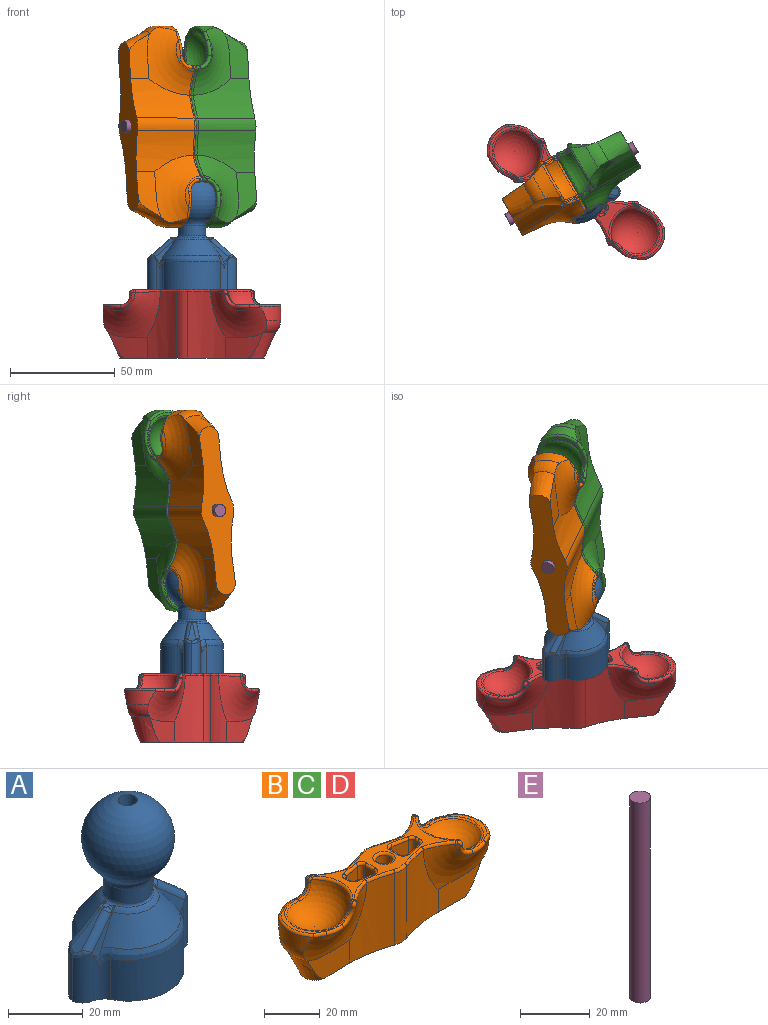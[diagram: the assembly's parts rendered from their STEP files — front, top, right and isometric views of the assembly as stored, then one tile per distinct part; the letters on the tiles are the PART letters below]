
ASSEMBLY  parts=5 mates=4
PART A: 86 faces, bbox 42.8x30.4x55.8 mm
  f0: plane 12.56x10.39mm, normal (0,-0.98,0.19), area 21.3mm2, adj f16,f23,f29,f42,f45,f46,f71,f72
  f1: plane 12.56x10.39mm, normal (0,0.98,0.19), area 21.3mm2, adj f13,f24,f32,f40,f61,f62,f79,f80
  f2: plane 1.84x1.78mm, normal (0,0,1), area 2.6mm2, adj f22,f46,f47,f48,f49,f50
  f3: bspline ~18.33x15.88mm, area 330.1mm2, adj f5,f8,f9,f11
  f4: bspline ~18.33x15.88mm, area 304.7mm2, adj f5,f8,f9,f11
  f5: cylinder r=6.94mm len=14.55mm, axis (0,0,-1), area 174.4mm2, adj f3,f4,f9,f11
  f6: cylinder r=15mm len=26.79mm, axis (0,0,-1), area 441.6mm2, adj f10,f25,f26,f33
  f7: cylinder r=15mm len=26.79mm, axis (0,0,-1), area 441.6mm2, adj f10,f27,f28,f30
  f8: cylinder r=7.94mm len=15.88mm, axis (0,0,-1), area 333.9mm2, adj f3,f4,f9,f10,f11
  f9: plane 1.5x1mm, normal (0,-1,0), area 1.1mm2, adj f3,f4,f5,f8
  f10: plane 42.34x30mm, normal (0,0,-1), area 600.2mm2, adj f6,f7,f8,f25,f26,f27,f28,f35
  f11: plane 15.57x15.31mm, normal (0,0,-1), area 176.5mm2, adj f3,f4,f5,f8
  f12: plane 1.98x1.91mm, normal (0,0,1), area 2.6mm2, adj f22,f57,f58,f59,f60,f61
  f13: bspline ~28.91x12.94mm, area 275.1mm2, adj f1,f18,f24,f32,f33,f34
  f14: plane 10.41x9.05mm, normal (-0.66,0,0.75), area 28.4mm2, adj f39,f40,f59,f76,f77
  f15: plane 12.57x10.39mm, normal (0,-0.98,0.19), area 21.3mm2, adj f16,f23,f31,f39,f56,f57,f73,f74
  f16: bspline ~28.91x12.94mm, area 275.1mm2, adj f0,f15,f23,f29,f30,f31
  f17: plane 10.41x9.05mm, normal (0.66,0,0.75), area 28.4mm2, adj f41,f42,f48,f68,f69
  f18: plane 12.57x10.39mm, normal (0,0.98,0.19), area 21.3mm2, adj f13,f24,f34,f41,f50,f51,f65,f66
  f19: cylinder r=6.5mm len=13mm, axis (0,0,-1), area 191.6mm2, adj f21,f22
  f20: sphere r=12.5mm, area 1728.4mm2, adj f21,f81
  f21: torus R=9.9mm, axis (0,0,1), area 133.2mm2, adj f19,f20
  f22: torus R=7.44mm, axis (0,0,1), area 43.2mm2, adj f2,f12,f19,f23,f24,f43,f44,f45
  f23: bspline ~16.51x7.87mm, area 37.6mm2, adj f0,f15,f16,f22,f43,f44,f54,f55
  f24: bspline ~16.51x7.87mm, area 37.6mm2, adj f1,f13,f18,f22,f52,f53,f63,f64
  f25: cylinder r=5mm len=14.41mm, axis (0,0,-1), area 56.2mm2, adj f6,f10,f34,f35,f65
  f26: cylinder r=5mm len=14.41mm, axis (0,0,-1), area 56.2mm2, adj f6,f10,f32,f38,f80
  f27: cylinder r=5mm len=14.41mm, axis (0,0,-1), area 56.2mm2, adj f7,f10,f31,f37,f73
  f28: cylinder r=5mm len=14.41mm, axis (0,0,-1), area 56.2mm2, adj f7,f10,f29,f36,f72
  f29: bspline ~6.67x5.77mm, area 12.8mm2, adj f0,f16,f28,f30,f72
  f30: bspline ~27.53x9.91mm, area 104.2mm2, adj f7,f16,f29,f31
  f31: bspline ~6.67x5.77mm, area 12.8mm2, adj f15,f16,f27,f30,f73
  f32: bspline ~6.67x5.77mm, area 12.8mm2, adj f1,f13,f26,f33,f80
  f33: bspline ~27.53x9.91mm, area 104.2mm2, adj f6,f13,f32,f34
  f34: bspline ~6.67x5.77mm, area 12.8mm2, adj f13,f18,f25,f33,f65
  f35: cylinder r=5mm len=15.46mm, axis (0,0,-1), area 92.6mm2, adj f10,f25,f36,f66,f67,f68
  f36: cylinder r=5mm len=15.46mm, axis (0,0,-1), area 92.6mm2, adj f10,f28,f35,f69,f70,f71
  f37: cylinder r=5mm len=15.46mm, axis (0,0,-1), area 92.6mm2, adj f10,f27,f38,f74,f75,f76
  f38: cylinder r=5mm len=15.46mm, axis (0,0,-1), area 92.6mm2, adj f10,f26,f37,f77,f78,f79
  f39: cylinder r=2.17mm len=11.07mm, axis (-0.75,-0.13,-0.65), area 38.1mm2, adj f14,f15,f58,f75
  f40: cylinder r=2.17mm len=11.07mm, axis (0.75,-0.13,0.65), area 38.1mm2, adj f1,f14,f60,f78
  f41: cylinder r=2.17mm len=11.07mm, axis (-0.75,-0.13,0.65), area 38.1mm2, adj f17,f18,f49,f67
  f42: cylinder r=2.17mm len=11.07mm, axis (0.75,-0.13,-0.65), area 38.1mm2, adj f0,f17,f47,f70
  f43: bspline ~0.78x0.75mm, area 0.1mm2, adj f22,f23,f44
  f44: bspline ~0.96x0.73mm, area 0.2mm2, adj f22,f23,f43,f45
  f45: bspline ~1.46x1.03mm, area 0.5mm2, adj f0,f22,f44,f46
  f46: bspline ~1.57x1.46mm, area 1.4mm2, adj f0,f2,f45,f47
  f47: bspline ~2.07x1.82mm, area 3.1mm2, adj f2,f42,f46,f48
  f48: cylinder r=1.57mm len=1.03mm, axis (0,-1,0), area 0.5mm2, adj f2,f17,f47,f49
  f49: bspline ~2.22x2.15mm, area 3.1mm2, adj f2,f41,f48,f50
  f50: bspline ~1.54x1.27mm, area 1.4mm2, adj f2,f18,f49,f51
  f51: bspline ~1.46x1.03mm, area 0.5mm2, adj f18,f22,f50,f52
  f52: bspline ~0.96x0.73mm, area 0.2mm2, adj f22,f24,f51,f53
  f53: bspline ~1x0.94mm, area 0.1mm2, adj f22,f24,f52
  f54: bspline ~1x0.94mm, area 0.1mm2, adj f22,f23,f55
  f55: bspline ~0.96x0.73mm, area 0.2mm2, adj f22,f23,f54,f56
  f56: bspline ~1.46x1.03mm, area 0.5mm2, adj f15,f22,f55,f57
  f57: bspline ~1.56x1.37mm, area 1.4mm2, adj f12,f15,f56,f58
  f58: bspline ~2.15x1.82mm, area 3.1mm2, adj f12,f39,f57,f59
  f59: cylinder r=1.57mm len=1.03mm, axis (0,-1,0), area 0.5mm2, adj f12,f14,f58,f60
  f60: bspline ~2.22x2.15mm, area 3.1mm2, adj f12,f40,f59,f61
  f61: bspline ~1.57x1.48mm, area 1.4mm2, adj f1,f12,f60,f62
  f62: bspline ~1.46x1.03mm, area 0.5mm2, adj f1,f22,f61,f63
  f63: bspline ~0.96x0.73mm, area 0.2mm2, adj f22,f24,f62,f64
  f64: bspline ~0.78x0.75mm, area 0.1mm2, adj f22,f24,f63
  f65: bspline ~8.8x3.81mm, area 2.3mm2, adj f18,f25,f34,f66
  f66: bspline ~1.36x1.32mm, area 0.8mm2, adj f18,f35,f65,f67
  f67: bspline ~2.98x2.85mm, area 2.6mm2, adj f35,f41,f66,f68
  f68: bspline ~3.29x2.24mm, area 4.8mm2, adj f17,f35,f67,f69
  f69: bspline ~3.29x2.24mm, area 4.8mm2, adj f17,f36,f68,f70
  f70: bspline ~2.98x2.85mm, area 2.6mm2, adj f36,f42,f69,f71
  f71: bspline ~1.36x1.32mm, area 0.8mm2, adj f0,f36,f70,f72
  f72: bspline ~8.8x3.81mm, area 2.3mm2, adj f0,f28,f29,f71
  f73: bspline ~8.8x3.81mm, area 2.3mm2, adj f15,f27,f31,f74
  f74: bspline ~1.36x1.32mm, area 0.8mm2, adj f15,f37,f73,f75
  f75: bspline ~2.98x2.85mm, area 2.6mm2, adj f37,f39,f74,f76
  f76: bspline ~3.29x2.24mm, area 4.8mm2, adj f14,f37,f75,f77
  f77: bspline ~3.29x2.24mm, area 4.8mm2, adj f14,f38,f76,f78
  f78: bspline ~2.98x2.85mm, area 2.6mm2, adj f38,f40,f77,f79
  f79: bspline ~1.36x1.32mm, area 0.8mm2, adj f1,f38,f78,f80
  f80: bspline ~8.8x3.81mm, area 2.3mm2, adj f1,f26,f32,f79
  f81: cone r=2.85mm half-angle=3.8deg, axis (0,0,1), area 77.3mm2, adj f20,f82
  f82: sphere r=7.5mm, area 685.5mm2, adj f81,f83
  f83: cone r=2.85mm half-angle=3.8deg, axis (0,0,1), area 75.2mm2, adj f82,f84
  f84: cone r=0.13mm half-angle=0.1deg, axis (0,0,1), area 5.8mm2, adj f83,f85
  f85: sphere r=7.5mm, area 0mm2, adj f84
PART B: 146 faces, bbox 113x30x32.8 mm
  f0: sphere r=15mm, area 23.2mm2, adj f22,f89,f91,f93,f95,f97
  f1: sphere r=15mm, area 23.2mm2, adj f20,f109,f110,f111,f112,f113
  f2: sphere r=12.5mm, area 560.4mm2, adj f114,f115,f116,f117,f118,f119,f120,f121
  f3: sphere r=15mm, area 23.2mm2, adj f23,f78,f79,f80,f81,f82
  f4: sphere r=15mm, area 23.2mm2, adj f21,f94,f96,f98,f100,f102
  f5: sphere r=12.5mm, area 560.4mm2, adj f70,f71,f72,f73,f74,f75,f76,f77
  f6: cylinder r=9mm len=31.5mm, axis (0,0,-1), area 196.5mm2, adj f24,f26,f103,f143
  f7: cylinder r=13.27mm len=18.19mm, axis (0,0,-1), area 103mm2, adj f18,f22,f23,f83,f85,f87
  f8: cylinder r=9mm len=31.5mm, axis (0,0,-1), area 196.5mm2, adj f25,f27,f88,f143
  f9: cylinder r=13.27mm len=18.19mm, axis (0,0,-1), area 103mm2, adj f19,f20,f21,f104,f106,f108
  f10: cylinder r=3mm len=31.5mm, axis (0,0,-1), area 593.8mm2, adj f138,f143
  f11: plane 52.62x21.86mm, normal (0,0,1), area 310.7mm2, adj f66,f67,f68,f69,f74,f82,f84,f86
  f12: plane 0.68x0.31mm, normal (1,0,0), area 0.2mm2, adj f30,f68,f70,f98
  f13: plane 0.68x0.31mm, normal (1,0,0), area 0.2mm2, adj f29,f67,f77,f113
  f14: plane 22.98x14.27mm, normal (0,0,1), area 40.1mm2, adj f29,f30,f73,f102,f104,f106,f108,f110
  f15: plane 0.68x0.31mm, normal (-1,0,0), area 0.2mm2, adj f31,f69,f93,f121
  f16: plane 0.68x0.31mm, normal (-1,0,0), area 0.2mm2, adj f28,f66,f78,f114
  f17: plane 22.98x14.27mm, normal (0,0,1), area 40.1mm2, adj f28,f31,f81,f83,f85,f87,f89,f118
  f18: torus R=5.27mm, axis (0,0,1), area 77.7mm2, adj f7,f22,f23,f144
  f19: torus R=5.27mm, axis (0,0,1), area 77.7mm2, adj f9,f20,f21,f145
  f20: torus R=26.08mm, axis (0,-1,0), area 502.5mm2, adj f1,f9,f19,f26,f107,f108,f141,f145
  f21: torus R=26.08mm, axis (0,-1,0), area 502.5mm2, adj f4,f9,f19,f27,f92,f104,f142,f145
  f22: torus R=26.08mm, axis (0,-1,0), area 502.5mm2, adj f0,f7,f18,f24,f87,f99,f140,f144
  f23: torus R=26.08mm, axis (0,-1,0), area 502.5mm2, adj f3,f7,f18,f25,f83,f84,f139,f144
  f24: cylinder r=58.26mm len=31.5mm, axis (0,0,-1), area 507.2mm2, adj f6,f22,f99,f101,f140,f143
  f25: cylinder r=58.26mm len=31.5mm, axis (0,0,-1), area 507.2mm2, adj f8,f23,f84,f86,f139,f143
  f26: cylinder r=58.26mm len=31.5mm, axis (0,0,-1), area 507.2mm2, adj f6,f20,f105,f107,f141,f143
  f27: cylinder r=58.26mm len=31.5mm, axis (0,0,-1), area 507.2mm2, adj f8,f21,f90,f92,f142,f143
  f28: cylinder r=5mm len=5mm, axis (0,1,0), area 5mm2, adj f16,f17,f79,f116
  f29: cylinder r=5mm len=5mm, axis (0,-1,0), area 5mm2, adj f13,f14,f76,f112
  f30: cylinder r=5mm len=5mm, axis (0,-1,0), area 5mm2, adj f12,f14,f71,f100
  f31: cylinder r=5mm len=5mm, axis (0,1,0), area 5mm2, adj f15,f17,f91,f120
  f32: plane 12.31x7.2mm, normal (-0.19,0.98,0), area 90.3mm2, adj f44,f50,f53,f135
  f33: plane 12.31x1.56mm, normal (-1,0,0), area 19.2mm2, adj f47,f51,f53,f131
  f34: plane 12.31x7.2mm, normal (-0.19,-0.98,0), area 90.3mm2, adj f42,f46,f47,f132
  f35: plane 12.31x4.39mm, normal (1,0,0), area 54mm2, adj f42,f44,f45,f136
  f36: plane 7.2x4.39mm, normal (0,0,1), area 21.4mm2, adj f45,f46,f50,f51
  f37: plane 12.31x7.2mm, normal (0.19,-0.98,0), area 90.3mm2, adj f59,f63,f65,f128
  f38: plane 12.31x1.56mm, normal (1,0,0), area 19.2mm2, adj f54,f58,f59,f127
  f39: plane 12.31x7.2mm, normal (0.19,0.98,0), area 90.3mm2, adj f54,f56,f57,f123
  f40: plane 12.31x4.39mm, normal (-1,0,0), area 54mm2, adj f56,f62,f65,f124
  f41: plane 7.2x4.39mm, normal (0,0,1), area 21.4mm2, adj f57,f58,f62,f63
  f42: cylinder r=1.69mm len=12.31mm, axis (0,0,-1), area 36.7mm2, adj f34,f35,f43,f134
  f43: sphere r=1.69mm, area 6.5mm2, adj f42,f45,f46
  f44: cylinder r=1.69mm len=12.31mm, axis (0,0,-1), area 36.7mm2, adj f32,f35,f48,f137
  f45: cylinder r=1.69mm len=4.39mm, axis (0,-1,0), area 11.7mm2, adj f35,f36,f43,f48
  f46: cylinder r=1.69mm len=7.53mm, axis (-0.98,0.19,0), area 19.5mm2, adj f34,f36,f43,f49
  f47: cylinder r=1.69mm len=12.31mm, axis (0,0,-1), area 28.6mm2, adj f33,f34,f49,f130
  f48: sphere r=1.69mm, area 5mm2, adj f44,f45,f50
  f49: sphere r=1.69mm, area 4.1mm2, adj f46,f47,f51
  f50: cylinder r=1.69mm len=7.53mm, axis (0.98,0.19,0), area 19.5mm2, adj f32,f36,f48,f52
  f51: cylinder r=1.69mm len=1.69mm, axis (0,1,0), area 4.1mm2, adj f33,f36,f49,f52
  f52: sphere r=1.69mm, area 3.9mm2, adj f50,f51,f53
  f53: cylinder r=1.69mm len=12.31mm, axis (0,0,-1), area 28.6mm2, adj f32,f33,f52,f133
  f54: cylinder r=1.69mm len=12.31mm, axis (0,0,-1), area 28.6mm2, adj f38,f39,f55,f125
  f55: sphere r=1.69mm, area 3.9mm2, adj f54,f57,f58
  f56: cylinder r=1.69mm len=12.31mm, axis (0,0,-1), area 36.7mm2, adj f39,f40,f60,f122
  f57: cylinder r=1.69mm len=7.53mm, axis (0.98,-0.19,0), area 19.5mm2, adj f39,f41,f55,f60
  f58: cylinder r=1.69mm len=1.69mm, axis (0,-1,0), area 4.1mm2, adj f38,f41,f55,f61
  f59: cylinder r=1.69mm len=12.31mm, axis (0,0,-1), area 28.6mm2, adj f37,f38,f61,f129
  f60: sphere r=1.69mm, area 6.7mm2, adj f56,f57,f62
  f61: sphere r=1.69mm, area 5.8mm2, adj f58,f59,f63
  f62: cylinder r=1.69mm len=4.39mm, axis (0,1,0), area 11.7mm2, adj f40,f41,f60,f64
  f63: cylinder r=1.69mm len=7.53mm, axis (-0.98,-0.19,0), area 19.5mm2, adj f37,f41,f61,f64
  f64: sphere r=1.69mm, area 4.8mm2, adj f62,f63,f65
  f65: cylinder r=1.69mm len=12.31mm, axis (0,0,-1), area 36.7mm2, adj f37,f40,f64,f126
  f66: cylinder r=1.69mm len=1.69mm, axis (0,1,0), area 1.7mm2, adj f11,f16,f80,f115
  f67: cylinder r=1.69mm len=1.69mm, axis (0,-1,0), area 1.7mm2, adj f11,f13,f75,f111
  f68: cylinder r=1.69mm len=1.69mm, axis (0,-1,0), area 1.7mm2, adj f11,f12,f72,f96
  f69: cylinder r=1.69mm len=1.69mm, axis (0,1,0), area 1.7mm2, adj f11,f15,f95,f119
  f70: torus R=10.87mm, axis (1,0,0), area 0.3mm2, adj f5,f12,f71,f72
  f71: bspline ~6.82x6.82mm, area 7.3mm2, adj f5,f30,f70,f73
  f72: bspline ~2.15x2.12mm, area 2.2mm2, adj f5,f68,f70,f74
  f73: torus R=10.87mm, axis (0,0,1), area 34.3mm2, adj f5,f14,f71,f76
  f74: torus R=13.46mm, axis (0,0,-1), area 33.4mm2, adj f5,f11,f72,f75
  f75: bspline ~2.12x1.9mm, area 2.2mm2, adj f5,f67,f74,f77
  f76: bspline ~6.82x6.82mm, area 7.3mm2, adj f5,f29,f73,f77
  f77: torus R=10.87mm, axis (1,0,0), area 0.3mm2, adj f5,f13,f75,f76
  f78: torus R=11.49mm, axis (-1,0,0), area 0.7mm2, adj f3,f16,f79,f80
  f79: bspline ~7.89x6.86mm, area 19.3mm2, adj f3,f28,f78,f81
  f80: bspline ~2.73x2.7mm, area 4.9mm2, adj f3,f66,f78,f82
  f81: torus R=11.49mm, axis (0,0,1), area 16.3mm2, adj f3,f17,f79,f83
  f82: torus R=13.96mm, axis (0,0,-1), area 1.4mm2, adj f3,f11,f80,f84
  f83: bspline ~6.48x4.72mm, area 10mm2, adj f7,f17,f23,f81,f85
  f84: bspline ~15.62x8.45mm, area 19.9mm2, adj f11,f23,f25,f82,f86
  f85: torus R=12.27mm, axis (0,0,1), area 30.3mm2, adj f7,f17,f83,f87
  f86: torus R=59.26mm, axis (0,0,-1), area 18.6mm2, adj f11,f25,f84,f88
  f87: bspline ~7.35x5.25mm, area 10mm2, adj f7,f17,f22,f85,f89
  f88: torus R=8mm, axis (0,0,-1), area 9.4mm2, adj f8,f11,f86,f90
  f89: torus R=11.49mm, axis (0,0,1), area 16.3mm2, adj f0,f17,f87,f91
  f90: torus R=59.26mm, axis (0,0,-1), area 18.6mm2, adj f11,f27,f88,f92
  f91: bspline ~7.89x7.89mm, area 19.3mm2, adj f0,f31,f89,f93
  f92: bspline ~15.62x8.45mm, area 19.9mm2, adj f11,f21,f27,f90,f94
  f93: torus R=11.49mm, axis (-1,0,0), area 0.7mm2, adj f0,f15,f91,f95
  f94: torus R=13.96mm, axis (0,0,-1), area 1.4mm2, adj f4,f11,f92,f96
  f95: bspline ~2.7x2.54mm, area 4.9mm2, adj f0,f69,f93,f97
  f96: bspline ~2.73x2.47mm, area 4.9mm2, adj f4,f68,f94,f98
  f97: torus R=13.96mm, axis (0,0,-1), area 1.4mm2, adj f0,f11,f95,f99
  f98: torus R=11.49mm, axis (1,0,0), area 0.7mm2, adj f4,f12,f96,f100
  f99: bspline ~15.62x8.45mm, area 19.9mm2, adj f11,f22,f24,f97,f101
  f100: bspline ~7.89x6.86mm, area 19.3mm2, adj f4,f30,f98,f102
  f101: torus R=59.26mm, axis (0,0,-1), area 18.6mm2, adj f11,f24,f99,f103
  f102: torus R=11.49mm, axis (0,0,1), area 16.3mm2, adj f4,f14,f100,f104
  f103: torus R=8mm, axis (0,0,-1), area 9.4mm2, adj f6,f11,f101,f105
  f104: bspline ~7.35x5.25mm, area 10mm2, adj f9,f14,f21,f102,f106
  f105: torus R=59.26mm, axis (0,0,-1), area 18.6mm2, adj f11,f26,f103,f107
  f106: torus R=12.27mm, axis (0,0,1), area 30.3mm2, adj f9,f14,f104,f108
  f107: bspline ~15.62x8.45mm, area 19.9mm2, adj f11,f20,f26,f105,f109
  f108: bspline ~6.48x4.72mm, area 10mm2, adj f9,f14,f20,f106,f110
  f109: torus R=13.96mm, axis (0,0,-1), area 1.4mm2, adj f1,f11,f107,f111
  f110: torus R=11.49mm, axis (0,0,1), area 16.3mm2, adj f1,f14,f108,f112
  f111: bspline ~2.72x2.7mm, area 4.9mm2, adj f1,f67,f109,f113
  f112: bspline ~7.89x7.89mm, area 19.3mm2, adj f1,f29,f110,f113
  f113: torus R=11.49mm, axis (1,0,0), area 0.7mm2, adj f1,f13,f111,f112
  f114: torus R=10.87mm, axis (-1,0,0), area 0.3mm2, adj f2,f16,f115,f116
  f115: bspline ~2.06x1.81mm, area 2.2mm2, adj f2,f66,f114,f117
  f116: bspline ~6.82x6.82mm, area 7.3mm2, adj f2,f28,f114,f118
  f117: torus R=13.46mm, axis (0,0,-1), area 33.4mm2, adj f2,f11,f115,f119
  f118: torus R=10.87mm, axis (0,0,1), area 34.3mm2, adj f2,f17,f116,f120
  f119: bspline ~2.12x1.9mm, area 2.2mm2, adj f2,f69,f117,f121
  f120: bspline ~6.82x6.82mm, area 7.3mm2, adj f2,f31,f118,f121
  f121: torus R=10.87mm, axis (-1,0,0), area 0.3mm2, adj f2,f15,f119,f120
  f122: torus R=2.69mm, axis (0,0,-1), area 5.7mm2, adj f11,f56,f123,f124
  f123: cylinder r=1mm len=7.39mm, axis (0.98,-0.19,0), area 11.5mm2, adj f11,f39,f122,f125
  f124: cylinder r=1mm len=4.39mm, axis (0,1,0), area 6.9mm2, adj f11,f40,f122,f126
  f125: torus R=2.69mm, axis (0,0,-1), area 4.4mm2, adj f11,f54,f123,f127
  f126: torus R=2.69mm, axis (0,0,-1), area 5.7mm2, adj f11,f65,f124,f128
  f127: cylinder r=1mm len=1.56mm, axis (0,-1,0), area 2.4mm2, adj f11,f38,f125,f129
  f128: cylinder r=1mm len=7.39mm, axis (-0.98,-0.19,0), area 11.5mm2, adj f11,f37,f126,f129
  f129: torus R=2.69mm, axis (0,0,-1), area 4.4mm2, adj f11,f59,f127,f128
  f130: torus R=2.69mm, axis (0,0,-1), area 4.4mm2, adj f11,f47,f131,f132
  f131: cylinder r=1mm len=1.56mm, axis (0,1,0), area 2.4mm2, adj f11,f33,f130,f133
  f132: cylinder r=1mm len=7.39mm, axis (-0.98,0.19,0), area 11.5mm2, adj f11,f34,f130,f134
  f133: torus R=2.69mm, axis (0,0,-1), area 4.4mm2, adj f11,f53,f131,f135
  f134: torus R=2.69mm, axis (0,0,-1), area 5.7mm2, adj f11,f42,f132,f136
  f135: cylinder r=1mm len=7.39mm, axis (0.98,0.19,0), area 11.5mm2, adj f11,f32,f133,f137
  f136: cylinder r=1mm len=4.39mm, axis (0,-1,0), area 6.9mm2, adj f11,f35,f134,f137
  f137: torus R=2.69mm, axis (0,0,-1), area 5.7mm2, adj f11,f44,f135,f136
  f138: torus R=4mm, axis (0,0,-1), area 33.2mm2, adj f10,f11
  f139: extruded ~21.73x11.82mm, area 181.8mm2, adj f23,f25,f143,f144
  f140: extruded ~21.73x11.82mm, area 181.8mm2, adj f22,f24,f143,f144
  f141: extruded ~21.73x11.82mm, area 181.8mm2, adj f20,f26,f143,f145
  f142: extruded ~21.73x11.82mm, area 181.8mm2, adj f21,f27,f143,f145
  f143: plane 80.67x18.1mm, normal (0,0,-1), area 903.7mm2, adj f6,f8,f10,f24,f25,f26,f27,f139
  f144: cone r=5.27mm half-angle=23.9deg, axis (0,0,1), area 156.2mm2, adj f18,f22,f23,f139,f140,f143
  f145: cone r=5.27mm half-angle=23.9deg, axis (0,0,1), area 156.2mm2, adj f19,f20,f21,f141,f142,f143
PART C: same geometry as B
PART D: same geometry as B
PART E: 3 faces, bbox 6x6x70 mm
  f0: cylinder r=3mm len=70mm, axis (0,0,-1), area 1319.5mm2, adj f1,f2
  f1: plane 6x6mm, normal (0,0,1), area 28.3mm2, adj f0
  f2: plane 6x6mm, normal (0,0,-1), area 28.3mm2, adj f0
PLACE A t=(-27.51,3.14,17.5)mm fixed
PLACE B rot(axis=(-0.68,-0.23,-0.7),164.3deg) t=(-49.2,-4.05,95.35)mm
PLACE C rot(axis=(0.18,-0.93,0.3),95.7deg) t=(-10.13,18.28,95.22)mm
PLACE D rot(axis=(0,0,-1),33.6deg) t=(-27.51,3.14,-5)mm
PLACE E rot(axis=(0.34,0.69,0.64),134deg) t=(-55.46,-18.34,85.31)mm
MATE fastened C.f6 <-> B.f6  axis (-0.87,-0.5,0) through (-29.67,7.12,95.28)mm
MATE ball A.f5 <-> B.f7  axis (0,0,1) through (-27.51,3.14,60.58)mm
MATE revolute D.f6 <-> A.f7  axis (0,0,1) through (-27.51,3.14,17.5)mm
MATE revolute E.f0 <-> B.f6  axis (-0.87,-0.5,0) through (-29.67,7.12,95.28)mm
